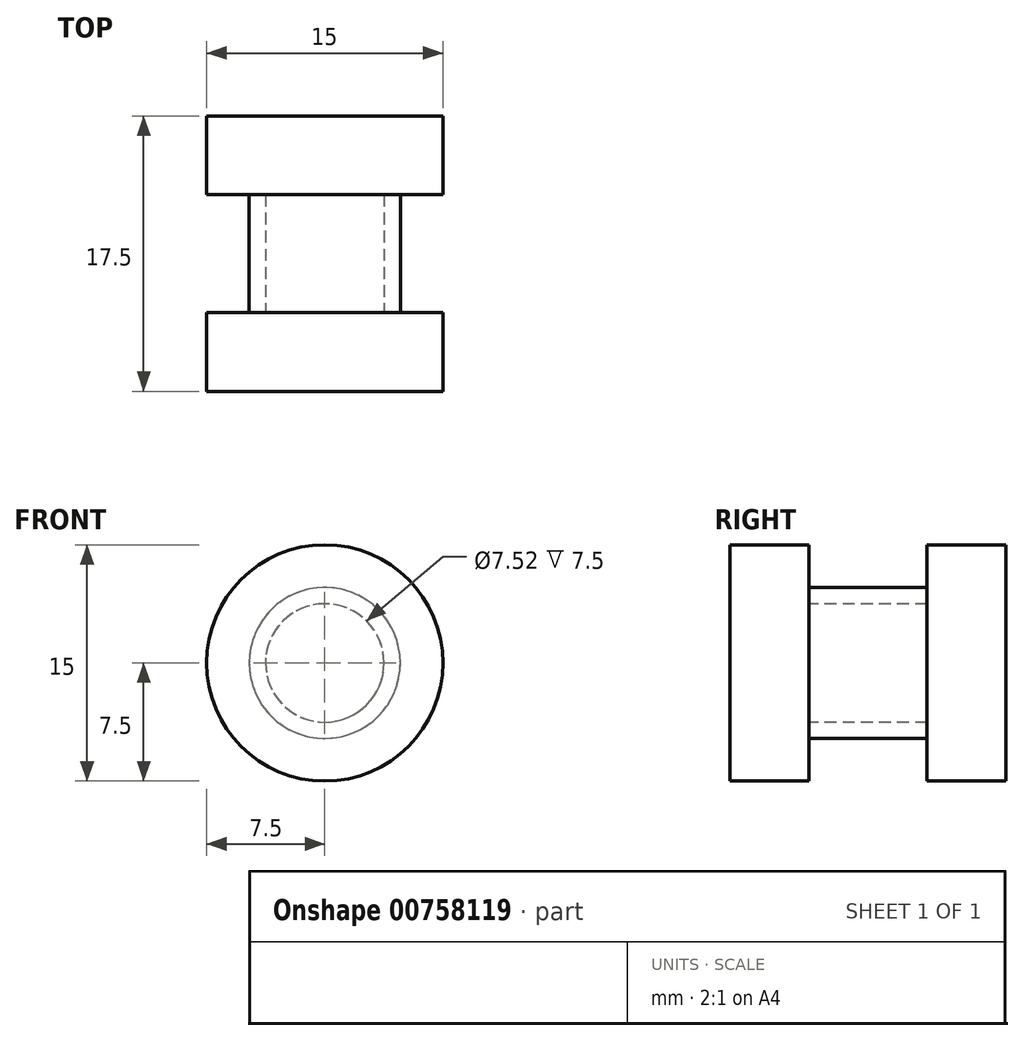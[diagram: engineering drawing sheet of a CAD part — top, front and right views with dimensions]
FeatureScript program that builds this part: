
annotation { "Feature Type Name" : "Feature", "Feature Type Description" : "" }
export const myFeature = defineFeature(function(context is Context, id is Id, definition is map)
    precondition{}
    {
        {
            var Q0;
            Q0=qCreatedBy(makeId("Front.planeOp"),FACE);
            var sketch = newSketch(context, id + "F0", { "sketchPlane" : qUnion([Q0])});
            skCircle(sketch, "E0", {"center": v(0, 0) * mm, "radius": 4.8 * mm});
            skSolve(sketch);
        }
        {
            var Q0;
            Q0 = qSketchRegion(id + "F0", true);
            extrude(context, id + "F1", {"entities" : qUnion([Q0]), "depth" : 25 * mm, "offsetDistance" : 25 * mm});
        }
        {
            var Q0;
            Q0=makeQuery(id+"F1.opExtrude","CAP_FACE",FACE,{"disambiguationData":[OSD([sQuery(id+"F0.wireOp",EDGE,"E0")])],"isStart":false});
            var sketch = newSketch(context, id + "F2", { "sketchPlane" : qUnion([Q0])});
            skCircle(sketch, "E1", {"center": v(0, 0) * mm, "radius": 3.76 * mm});
            skSolve(sketch);
        }
        {
            var Q0;
            Q0 = qSketchRegion(id + "F2", true);
            extrude(context, id + "F3", {"entities" : qUnion([Q0]), "operationType" : NewBodyOperationType.REMOVE, "oppositeDirection" : true, "depth" : 31.2 * mm, "offsetDistance" : 25 * mm});
        }
        {
            var Q0;
            Q0=makeQuery(id+"F1.opExtrude","CAP_FACE",FACE,{"disambiguationData":[OSD([sQuery(id+"F0.wireOp",EDGE,"E0")])],"isStart":false});
            var sketch = newSketch(context, id + "F4", { "sketchPlane" : qUnion([Q0])});
            skCircle(sketch, "E2", {"center": v(0, 0) * mm, "radius": 4.8 * mm});
            skSolve(sketch);
        }
        {
            var Q0;
            Q0 = qSketchRegion(id + "F4", true);
            extrude(context, id + "F5", {"entities" : qUnion([Q0]), "operationType" : NewBodyOperationType.REMOVE, "oppositeDirection" : true, "depth" : 7.5 * mm, "offsetDistance" : 25 * mm});
        }
        {
            var Q0;
            Q0=makeQuery(id+"F5.boolean.opBoolean","COPY",FACE,{"derivedFrom":makeQuery(id+"F5.opExtrude","CAP_FACE",FACE,{"disambiguationData":[OSD([sQuery(id+"F4.wireOp",EDGE,"E2")])],"isStart":false})});
            var sketch = newSketch(context, id + "F6", { "sketchPlane" : qUnion([Q0])});
            skCircle(sketch, "E3", {"center": v(0, 0) * mm, "radius": 7.5 * mm});
            skSolve(sketch);
        }
        {
            var Q0;
            Q0 = qSketchRegion(id + "F6", true);
            extrude(context, id + "F7", {"entities" : qUnion([Q0]), "operationType" : NewBodyOperationType.ADD, "oppositeDirection" : true, "depth" : 5 * mm, "offsetDistance" : 25 * mm});
        }
        {
            var Q0;
            Q0=makeQuery(id+"F1.opExtrude","CAP_FACE",FACE,{"disambiguationData":[OSD([sQuery(id+"F0.wireOp",EDGE,"E0")])],"isStart":true});
            var sketch = newSketch(context, id + "F8", { "sketchPlane" : qUnion([Q0])});
            skCircle(sketch, "E4", {"center": v(0, 0) * mm, "radius": 7.5 * mm});
            skSolve(sketch);
        }
        {
            var Q0;
            Q0 = qSketchRegion(id + "F8", true);
            extrude(context, id + "F9", {"entities" : qUnion([Q0]), "operationType" : NewBodyOperationType.ADD, "oppositeDirection" : true, "depth" : 5 * mm, "offsetDistance" : 25 * mm});
        }
    });
